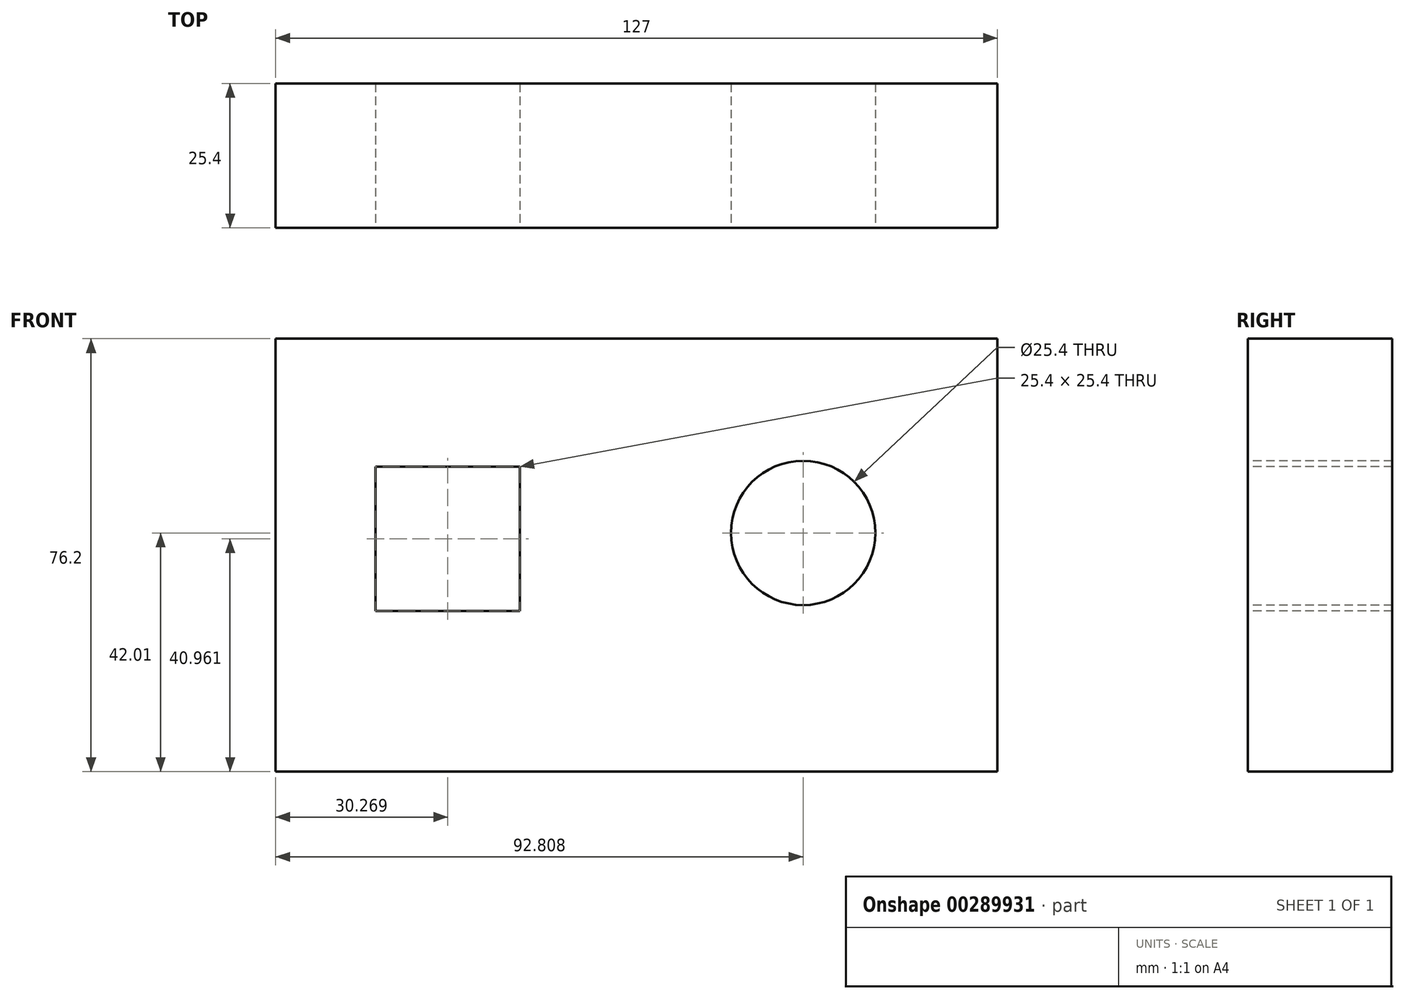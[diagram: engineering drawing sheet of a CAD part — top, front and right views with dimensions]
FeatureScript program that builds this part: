
annotation { "Feature Type Name" : "Feature", "Feature Type Description" : "" }
export const myFeature = defineFeature(function(context is Context, id is Id, definition is map)
    precondition{}
    {
        {
            var Q0;
            Q0=qCreatedBy(makeId("Front.planeOp"),FACE);
            var sketch = newSketch(context, id + "F0", { "sketchPlane" : qUnion([Q0])});
            skLineSegment(sketch, "E0.bottom", {"start": v(-55.19, 76.2) * mm, "end": v(71.81, 76.2) * mm});
            skLineSegment(sketch, "E0.top", {"start": v(-55.19, 0) * mm, "end": v(71.81, 0) * mm});
            skLineSegment(sketch, "E0.left", {"start": v(-55.19, 76.2) * mm, "end": v(-55.19, 0) * mm});
            skLineSegment(sketch, "E0.right", {"start": v(71.81, 76.2) * mm, "end": v(71.81, 0) * mm});
            skSolve(sketch);
        }
        {
            var Q0;
            Q0 = qSketchRegion(id + "F0", true);
            extrude(context, id + "F1", {"entities" : qUnion([Q0]), "depth" : 25.4 * mm});
        }
        {
            var Q0;
            Q0=makeQuery(id+"F1.opExtrude","CAP_FACE",FACE,{"disambiguationData":[OSD([sQuery(id+"F0.wireOp",EDGE,"E0.bottom"),sQuery(id+"F0.wireOp",EDGE,"E0.top"),sQuery(id+"F0.wireOp",EDGE,"E0.left"),sQuery(id+"F0.wireOp",EDGE,"E0.right")])],"isStart":false});
            var sketch = newSketch(context, id + "F2", { "sketchPlane" : qUnion([Q0])});
            skLineSegment(sketch, "E1.bottom", {"start": v(-37.62, 53.66) * mm, "end": v(-12.22, 53.66) * mm});
            skLineSegment(sketch, "E1.top", {"start": v(-37.62, 28.26) * mm, "end": v(-12.22, 28.26) * mm});
            skLineSegment(sketch, "E1.left", {"start": v(-37.62, 53.66) * mm, "end": v(-37.62, 28.26) * mm});
            skLineSegment(sketch, "E1.right", {"start": v(-12.22, 53.66) * mm, "end": v(-12.22, 28.26) * mm});
            skCircle(sketch, "E2", {"center": v(37.62, 42.01) * mm, "radius": 12.7 * mm});
            skSolve(sketch);
        }
        {
            var Q0;
            Q0 = qSketchRegion(id + "F2", true);
            extrude(context, id + "F3", {"entities" : qUnion([Q0]), "operationType" : NewBodyOperationType.REMOVE, "oppositeDirection" : true, "depth" : 25.4 * mm});
        }
    });
